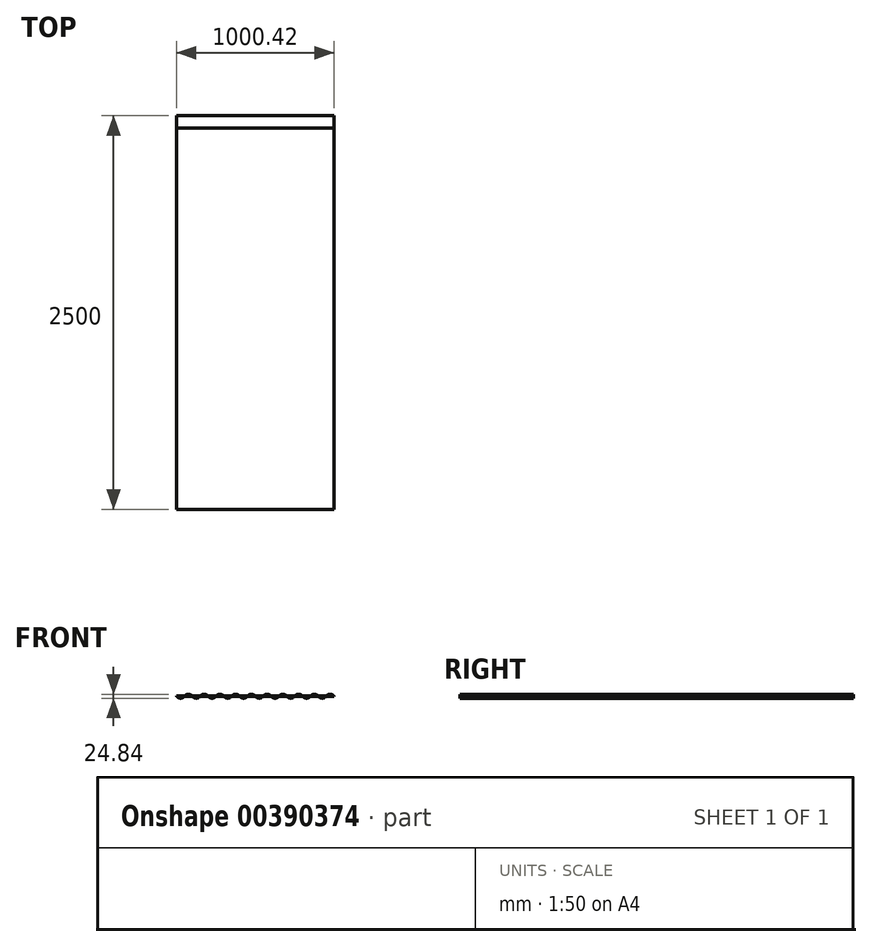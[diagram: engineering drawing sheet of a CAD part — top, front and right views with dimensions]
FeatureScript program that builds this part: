
annotation { "Feature Type Name" : "Feature", "Feature Type Description" : "" }
export const myFeature = defineFeature(function(context is Context, id is Id, definition is map)
    precondition{}
    {
        {
            var Q0;
            Q0=qCreatedBy(makeId("Front.planeOp"),FACE);
            var sketch = newSketch(context, id + "F0", { "sketchPlane" : qUnion([Q0])});
            skArc(sketch, "E0", {"start": v(-25, 0) * mm, "mid": v(0, -12.42) * mm, "end": v(25, 0) * mm});
            skLineSegment(sketch, "E1", {"start": v(25, 0) * mm, "end": v(25, 36.98) * mm, "construction": true});
            skArc(sketch, "E2.MirrorCS", {"start": v(75, 0) * mm, "mid": v(50, 12.42) * mm, "end": v(25, 0) * mm});
            skLineSegment(sketch, "E3", {"start": v(-25, 0) * mm, "end": v(975, 0) * mm, "construction": true});
            skArc(sketch, "E4.1.0.0", {"start": v(75, 0) * mm, "mid": v(100, -12.42) * mm, "end": v(125, 0) * mm});
            skArc(sketch, "E4.1.0.1", {"start": v(175, 0) * mm, "mid": v(150, 12.42) * mm, "end": v(125, 0) * mm});
            skArc(sketch, "E4.2.0.0", {"start": v(175, 0) * mm, "mid": v(200, -12.42) * mm, "end": v(225, 0) * mm});
            skArc(sketch, "E4.2.0.1", {"start": v(275, 0) * mm, "mid": v(250, 12.42) * mm, "end": v(225, 0) * mm});
            skArc(sketch, "E4.3.0.0", {"start": v(275, 0) * mm, "mid": v(300, -12.42) * mm, "end": v(325, 0) * mm});
            skArc(sketch, "E4.3.0.1", {"start": v(375, 0) * mm, "mid": v(350, 12.42) * mm, "end": v(325, 0) * mm});
            skArc(sketch, "E4.4.0.0", {"start": v(375, 0) * mm, "mid": v(400, -12.42) * mm, "end": v(425, 0) * mm});
            skArc(sketch, "E4.4.0.1", {"start": v(475, 0) * mm, "mid": v(450, 12.42) * mm, "end": v(425, 0) * mm});
            skArc(sketch, "E4.5.0.0", {"start": v(475, 0) * mm, "mid": v(500, -12.42) * mm, "end": v(525, 0) * mm});
            skArc(sketch, "E4.5.0.1", {"start": v(575, 0) * mm, "mid": v(550, 12.42) * mm, "end": v(525, 0) * mm});
            skArc(sketch, "E4.6.0.0", {"start": v(575, 0) * mm, "mid": v(600, -12.42) * mm, "end": v(625, 0) * mm});
            skArc(sketch, "E4.6.0.1", {"start": v(675, 0) * mm, "mid": v(650, 12.42) * mm, "end": v(625, 0) * mm});
            skArc(sketch, "E4.7.0.0", {"start": v(675, 0) * mm, "mid": v(700, -12.42) * mm, "end": v(725, 0) * mm});
            skArc(sketch, "E4.7.0.1", {"start": v(775, 0) * mm, "mid": v(750, 12.42) * mm, "end": v(725, 0) * mm});
            skArc(sketch, "E4.8.0.0", {"start": v(775, 0) * mm, "mid": v(800, -12.42) * mm, "end": v(825, 0) * mm});
            skArc(sketch, "E4.8.0.1", {"start": v(875, 0) * mm, "mid": v(850, 12.42) * mm, "end": v(825, 0) * mm});
            skArc(sketch, "E4.9.0.0", {"start": v(875, 0) * mm, "mid": v(900, -12.42) * mm, "end": v(925, 0) * mm});
            skArc(sketch, "E4.9.0.1", {"start": v(975, 0) * mm, "mid": v(950, 12.42) * mm, "end": v(925, 0) * mm});
            skLineSegment(sketch, "E4.direction1", {"start": v(-25, 0) * mm, "end": v(75, 0) * mm, "construction": true});
            skSolve(sketch);
        }
        {
            var Q0;
            Q0=sQuery(id+"F0.wireOp",EDGE,"E4.2.0.0");
            var Q1;
            Q1=sQuery(id+"F0.wireOp",EDGE,"E4.6.0.1");
            var Q2;
            Q2=sQuery(id+"F0.wireOp",EDGE,"E4.8.0.1");
            var Q3;
            Q3=sQuery(id+"F0.wireOp",EDGE,"E4.6.0.0");
            var Q4;
            Q4=sQuery(id+"F0.wireOp",EDGE,"E0");
            var Q5;
            Q5=sQuery(id+"F0.wireOp",EDGE,"E2.MirrorCS");
            var Q6;
            Q6=sQuery(id+"F0.wireOp",EDGE,"E4.9.0.1");
            var Q7;
            Q7=sQuery(id+"F0.wireOp",EDGE,"E4.1.0.0");
            var Q8;
            Q8=sQuery(id+"F0.wireOp",EDGE,"E4.7.0.1");
            var Q9;
            Q9=sQuery(id+"F0.wireOp",EDGE,"E4.5.0.1");
            var Q10;
            Q10=sQuery(id+"F0.wireOp",EDGE,"E4.1.0.1");
            var Q11;
            Q11=sQuery(id+"F0.wireOp",EDGE,"E4.2.0.1");
            var Q12;
            Q12=sQuery(id+"F0.wireOp",EDGE,"E4.3.0.0");
            var Q13;
            Q13=sQuery(id+"F0.wireOp",EDGE,"E4.3.0.1");
            var Q14;
            Q14=sQuery(id+"F0.wireOp",EDGE,"E4.4.0.0");
            var Q15;
            Q15=sQuery(id+"F0.wireOp",EDGE,"E4.4.0.1");
            var Q16;
            Q16=sQuery(id+"F0.wireOp",EDGE,"E4.5.0.0");
            var Q17;
            Q17=sQuery(id+"F0.wireOp",EDGE,"E4.9.0.0");
            var Q18;
            Q18=sQuery(id+"F0.wireOp",EDGE,"E4.8.0.0");
            var Q19;
            Q19=sQuery(id+"F0.wireOp",EDGE,"E4.7.0.0");
            extrude(context, id + "F1", {"bodyType" : ToolBodyType.SURFACE, "operationType" : NewBodyOperationType.ADD, "surfaceEntities" : qUnion([Q0, Q1, Q2, Q3, Q4, Q5, Q6, Q7, Q8, Q9, Q10, Q11, Q12, Q13, Q14, Q15, Q16, Q17, Q18, Q19]), "depth" : 2500 * mm});
        }
        {
            var Q0;
            Q0=qCreatedBy(makeId("Top.planeOp"),FACE);
            var sketch = newSketch(context, id + "F2", { "sketchPlane" : qUnion([Q0])});
            skLineSegment(sketch, "E5.bottom", {"start": v(-25.25, 0) * mm, "end": v(975.17, 0) * mm});
            skLineSegment(sketch, "E5.top", {"start": v(-25.25, -78.33) * mm, "end": v(975.17, -78.33) * mm});
            skLineSegment(sketch, "E5.left", {"start": v(-25.25, 0) * mm, "end": v(-25.25, -78.33) * mm});
            skLineSegment(sketch, "E5.right", {"start": v(975.17, 0) * mm, "end": v(975.17, -78.33) * mm});
            skSolve(sketch);
        }
        {
            var Q0;
            Q0=makeQuery(id+"F2.imprint","IMPRINT",FACE,{"disambiguationData":[TD([[makeQuery(id+"F2.imprint","IMPRINT",EDGE,{"derivedFrom":sQuery(id+"F2.wireOp",EDGE,"E5.bottom")}),-1.0]])]});
            var Q1;
            Q1=sQuery(id+"F2.wireOp",EDGE,"E5.bottom");
            var Q2;
            Q2=sQuery(id+"F2.wireOp",EDGE,"E5.right");
            var Q3;
            Q3=sQuery(id+"F2.wireOp",EDGE,"E5.top");
            var Q4;
            Q4=sQuery(id+"F2.wireOp",EDGE,"E5.left");
            extrude(context, id + "F3", {"entities" : qUnion([Q0]), "bodyType" : ToolBodyType.SURFACE, "surfaceEntities" : qUnion([Q1, Q2, Q3, Q4]), "depth" : 1 * mm});
        }
    });
